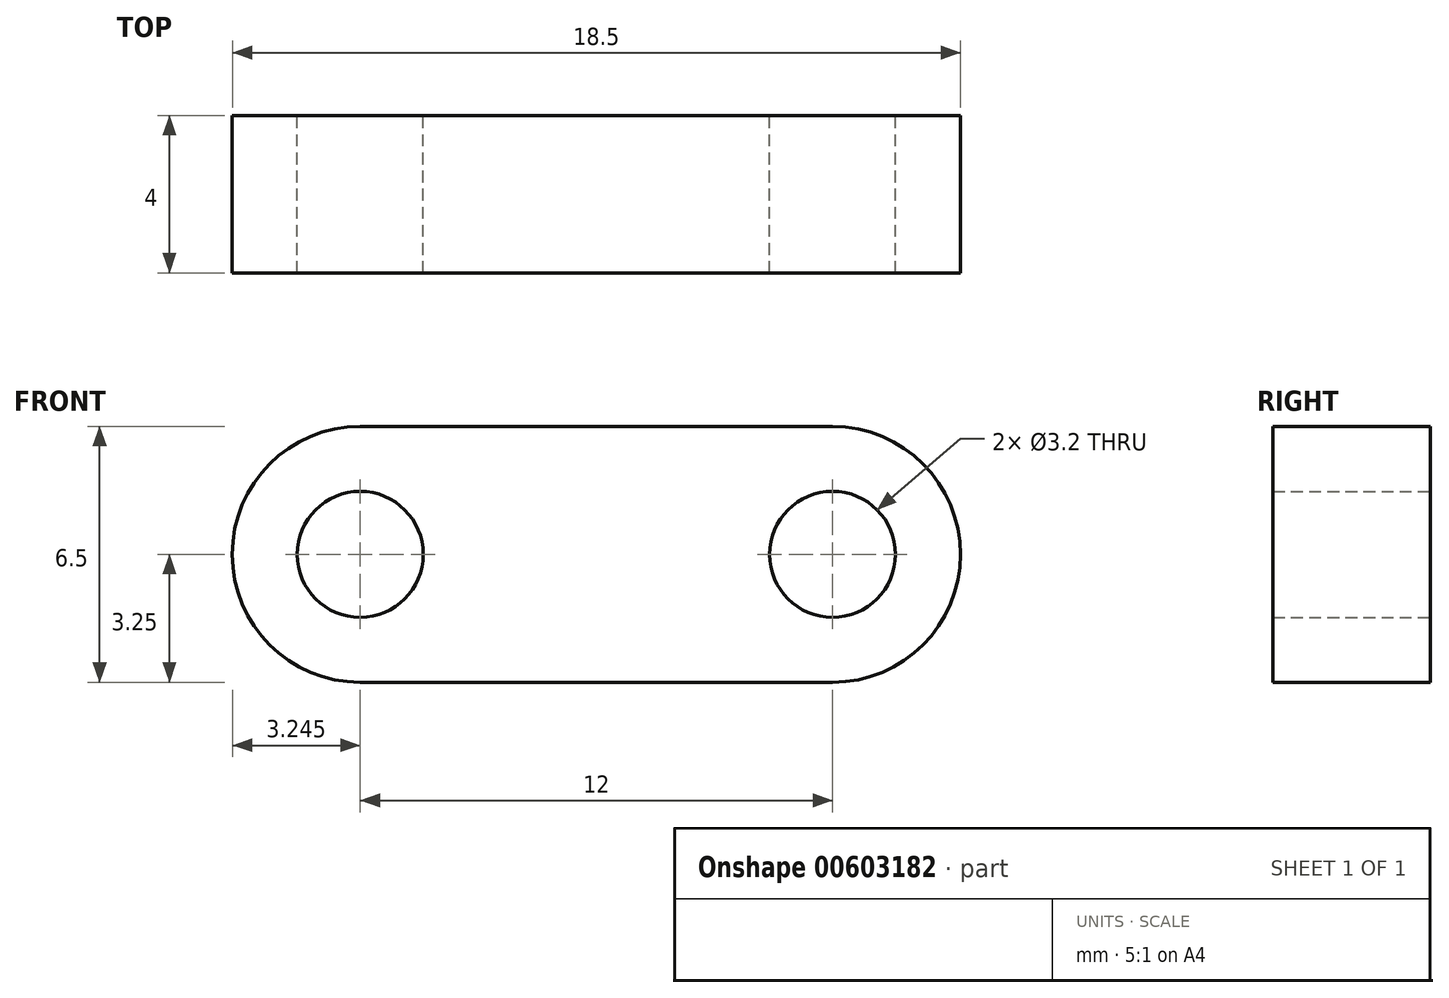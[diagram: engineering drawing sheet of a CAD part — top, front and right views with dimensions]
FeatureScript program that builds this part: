
annotation { "Feature Type Name" : "Feature", "Feature Type Description" : "" }
export const myFeature = defineFeature(function(context is Context, id is Id, definition is map)
    precondition{}
    {
        {
            var Q0;
            Q0=qCreatedBy(makeId("Front.planeOp"),FACE);
            var sketch = newSketch(context, id + "F0", { "sketchPlane" : qUnion([Q0])});
            skCircle(sketch, "E0.1.0", {"center": v(-6.6, 7.49) * mm, "radius": 1.6 * mm});
            skCircle(sketch, "E1.MirrorC", {"center": v(5.4, 7.49) * mm, "radius": 1.6 * mm});
            skLineSegment(sketch, "E2", {"start": v(-6.6, 10.74) * mm, "end": v(5.4, 10.74) * mm});
            skLineSegment(sketch, "E3", {"start": v(-6.6, 4.24) * mm, "end": v(5.4, 4.24) * mm});
            skArc(sketch, "E4", {"start": v(5.4, 10.74) * mm, "mid": v(8.65, 7.49) * mm, "end": v(5.4, 4.24) * mm});
            skArc(sketch, "E5", {"start": v(-6.6, 10.74) * mm, "mid": v(-9.85, 7.49) * mm, "end": v(-6.6, 4.24) * mm});
            skSolve(sketch);
        }
        {
            var Q0;
            Q0=makeQuery(id+"F0.imprint","IMPRINT",FACE,{"disambiguationData":[TD([[makeQuery(id+"F0.imprint","IMPRINT",EDGE,{"derivedFrom":sQuery(id+"F0.wireOp",EDGE,"E0.1.0")}),-1.0]])]});
            extrude(context, id + "F1", {"entities" : qUnion([Q0]), "depth" : 4 * mm, "offsetDistance" : 25 * mm});
        }
    });
